# Revit family: Dock_Ladder_Kattsafe_Parapet
name_source: partatom
category: Specialty Equipment
units: mm (PartAtom-declared; Revit-internal decimal feet)

## family parameters
Always vertical = No
Cut with Voids When Loaded = No
Enable Cutting in Views = No
Maintain Annotation Orientation = No
OmniClass Number = 23.17.23.15
Part Type = Normal
Room Calculation Point = No
Round Connector Dimension = Use Diameter
Shared = No
Work Plane-Based = Yes

## types (1)
- RL452
    Assembly Code = E1090100
    Default Elevation = 1219 mm
    Description = The RL452 ladder dock - parapet mount - provides a secure attachment point for portable ladders used by maintenance personnel when accessing elevated areas.
    ElementType = Ladder
    Export Type to IFC As = IfcBuildingElementProxy
    IfcExportAs = IfcBuildingElementProxy
    IfcExportType = USERDEFINED
    LadderHeight = 856 mm
    Manufacturer = Kattsafe®
    ManufacturerOverallWidth = 801 mm  [stored 2.62795 ft]
    ManufacturerSpecCode = RL452
    ManufacturerURLProductSpecific = https://kattsafe.com.au
    Model = RL452
    ModifiedIssue = 20250224 $
    Type Comments = Dock - Parapet - Ladder
    Type IFC Predefined Type = USERDEFINED
    URL = https://kattsafe.com.au
    Uniclass2015Code = Pr_25_30_85_02
    Uniclass2015Title = Access ladders
    Uniclass2015Version = Products v1.35

note: [stored X ft] marks values corroborated as IEEE doubles in the binary element streams (Revit-internal decimal feet)

## geometry (parser evidence)
native form markers: Sweep x7
no freeform markers — native parametric forms only
